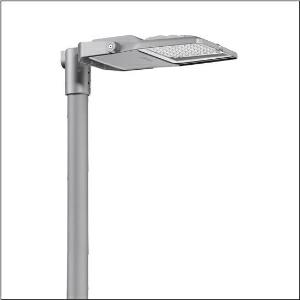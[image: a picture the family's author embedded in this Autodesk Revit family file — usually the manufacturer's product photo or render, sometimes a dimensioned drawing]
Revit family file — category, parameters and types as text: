
# Revit family: floodlight_fl_21_iq_mini___pl43_5xa7771b2a3a_6d21
name_source: partatom
category: Lighting Fixtures
units: mm (PartAtom-declared; Revit-internal decimal feet)

## family parameters
Cut with Voids When Loaded = No
Host = Face
Light Source = No
Part Type = Normal
Room Calculation Point = No
Round Connector Dimension = Use Diameter
Shared = No

## types (1)
- --- (1 x LED, 6400 lm, 45.5 W, 3000K)
    Apparent Load = 46 VA
    CIE Flux Codes = 27 78 99 100 100
    Color Rendering = 70
    Color Temperature = 3000K
    Default Elevation = 1800 mm
    Description = Floodlight FL 21 iQ mini, floodlight, primary light control with lens, of PMMA, primary optical cover: protective disc, of toughened safety glass, transparent, light distribution: PL43, light emission: direct distribution, installation type: surface-mounted, LED, High Power LED, rated luminous flux: 6.400lm, luminous efficacy: 141lm/W, light colour: 730, colour temperature: 3000K, control: Auto-Match, Temp-Guard, Lumen-Switch, Night-Set, Smart-Wire, Light-Fading, Desk-Remote (wireless, voltage-free reading and setting of iQ features in the workshop via application-optimized NFC function/RFID function), optimised constant luminous flux control (CLO 2.0), with terminal, 6-pole, mains connection: 220..240V, AC, 50/60Hz, start of lifetime: 46W, end of service life: 48W, reduction: 22W, luminaire housing, of diecast aluminium, powder-coated, Siteco® metallic grey (DB 702S), corrosivity category C5 mid according to DIN EN ISO 12944, sealing non-destructively replaceable, please order mast flange separately, mast bracket, of steel, galvanised, powder-coated, Siteco® metallic grey (DB 702S), protection rating (complete): IP66, insulation class (complete): insulation class II (safety insulation), certification: CE, ENEC, VDE, protection symbol: D, impact resistance: IK08, permissible operating ambient temperature: -40..+40°C, permissible operating ambient temperature for outdoor applications: -40..+50°C, standard: DIN EN 12944, LABS conformity tested according to VDMA 24364:2018-05, packaging unit: 1 piece

Light Distribution: PL43
    Height = 70 mm
    Lamp = 1 x LED
    Lamp Light Flux = 6400 lm
    Lamp Power = 45.5 W
    Lamp count = 1
    Length = 485 mm
    Luminous efficacy = 141 lm/W
    Manufacturer = Siteco
    ModVariant = No
    Model = 5XA7771B2A3A
    Number of Poles = 1
    OnlyDefault = Yes
    Power Factor = 1
    Product Name = Floodlight FL 21 iQ mini | PL43
    Product group = floodlight | pylon annexe
    ProductGroupID = 6200
    Protection Class = Protection class II
    Protection Degree = IP 66
    RLX_Detail_Level = 1
    RLX_Emergency_Light_Flux = 0 lm
    RLX_Emergency_Type = 0
    RLX_Emergency_Type_DB = No
    RlxData = <blob elided: 100953 chars, md5=59778743>
    Socket = socket
    Standby Power = 0 W
    System Light Flux = 6400 lm
    System Power = 46 W
    Type Comments = factory setting: luminous flux: 100 % | dim-lin: 254 | 463 mA
    Type Image = l_1007125.jpg
    URL = http://relux.com
    VarID = @adj_095305
    Voltage = 0 V
    Weight = 0.00 kg
    Width = 337 mm

## geometry (parser evidence)
native form markers: Blend x4, Sweep x10
no freeform markers — native parametric forms only
